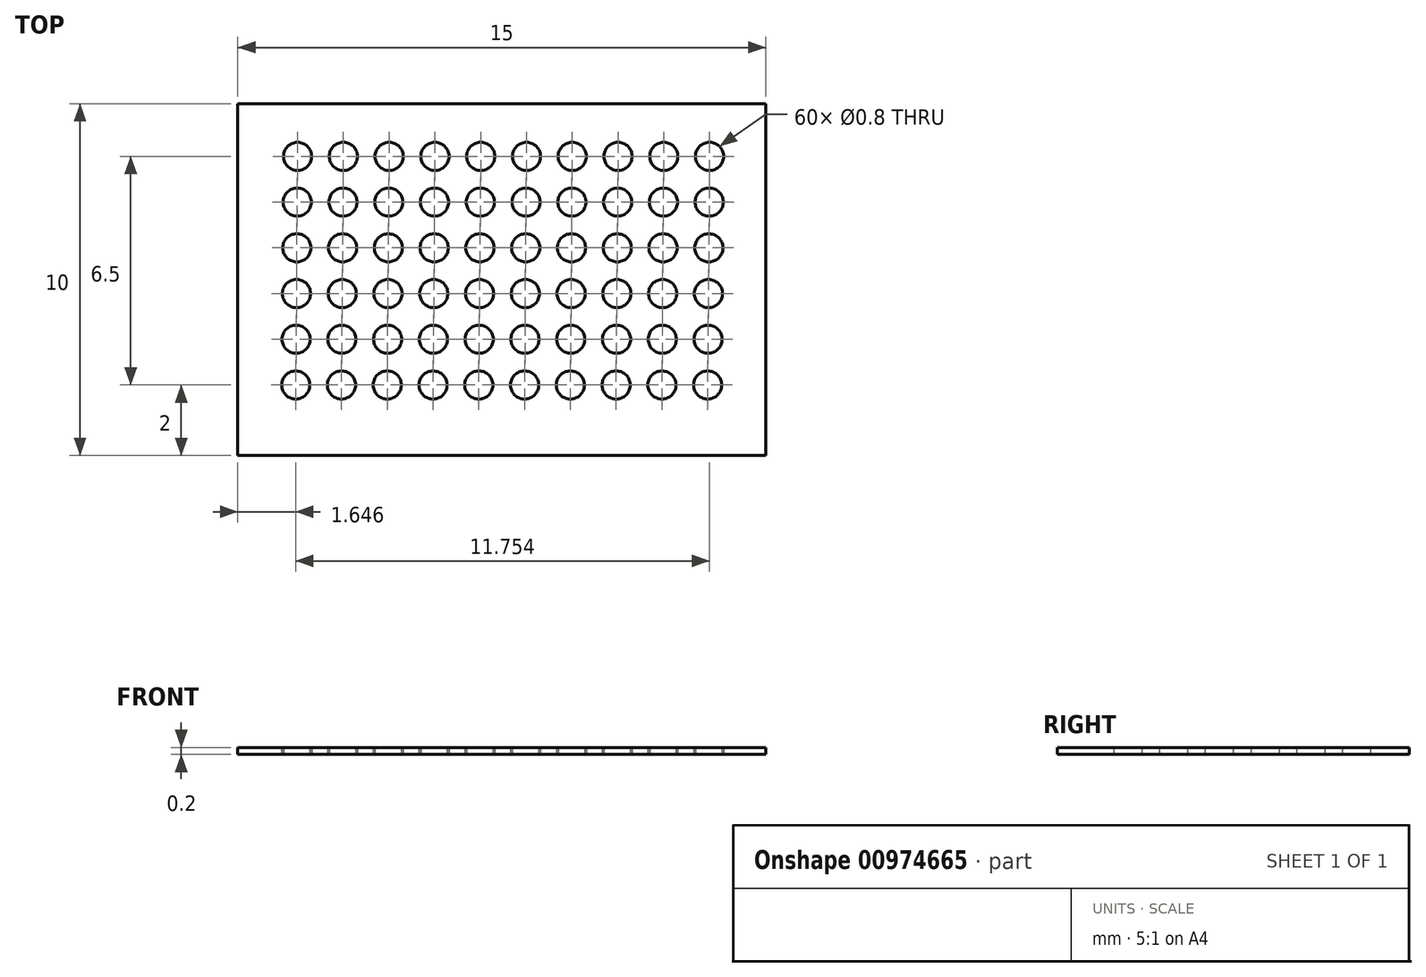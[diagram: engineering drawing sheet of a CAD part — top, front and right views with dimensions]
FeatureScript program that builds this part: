
annotation { "Feature Type Name" : "Feature", "Feature Type Description" : "" }
export const myFeature = defineFeature(function(context is Context, id is Id, definition is map)
    precondition{}
    {
        {
            var Q0;
            Q0=qCreatedBy(makeId("Top.planeOp"),FACE);
            var sketch = newSketch(context, id + "F0", { "sketchPlane" : qUnion([Q0])});
            skLineSegment(sketch, "E0.bottom", {"start": v(0, 0) * mm, "end": v(15, 0) * mm});
            skLineSegment(sketch, "E0.top", {"start": v(0, -10) * mm, "end": v(15, -10) * mm});
            skLineSegment(sketch, "E0.left", {"start": v(0, 0) * mm, "end": v(0, -10) * mm});
            skLineSegment(sketch, "E0.right", {"start": v(15, 0) * mm, "end": v(15, -10) * mm});
            skEllipse(sketch, "E1", {"center": v(1.7, -1.5) * mm, "majorRadius": 0.4 * mm, "minorRadius": 0.4 * mm, "majorAxis": v(0.93, 0.38)});
            skLineSegment(sketch, "E2.direction1", {"start": v(1.7, -1.5) * mm, "end": v(3, -1.5) * mm, "construction": true});
            skLineSegment(sketch, "E3.direction1", {"start": v(1.2, -1.1) * mm, "end": v(1.2, -2) * mm, "construction": true});
            skEllipse(sketch, "E4.0.1.0", {"center": v(3, -1.5) * mm, "majorRadius": 0.4 * mm, "minorRadius": 0.4 * mm, "majorAxis": v(0.93, 0.38)});
            skEllipse(sketch, "E4.0.2.0", {"center": v(4.3, -1.5) * mm, "majorRadius": 0.4 * mm, "minorRadius": 0.4 * mm, "majorAxis": v(0.93, 0.38)});
            skEllipse(sketch, "E4.0.3.0", {"center": v(5.6, -1.5) * mm, "majorRadius": 0.4 * mm, "minorRadius": 0.4 * mm, "majorAxis": v(0.93, 0.38)});
            skEllipse(sketch, "E4.0.4.0", {"center": v(6.9, -1.5) * mm, "majorRadius": 0.4 * mm, "minorRadius": 0.4 * mm, "majorAxis": v(0.93, 0.38)});
            skEllipse(sketch, "E4.0.5.0", {"center": v(8.2, -1.5) * mm, "majorRadius": 0.4 * mm, "minorRadius": 0.4 * mm, "majorAxis": v(0.93, 0.38)});
            skEllipse(sketch, "E4.0.6.0", {"center": v(9.5, -1.5) * mm, "majorRadius": 0.4 * mm, "minorRadius": 0.4 * mm, "majorAxis": v(0.93, 0.38)});
            skEllipse(sketch, "E4.0.7.0", {"center": v(10.8, -1.5) * mm, "majorRadius": 0.4 * mm, "minorRadius": 0.4 * mm, "majorAxis": v(0.93, 0.38)});
            skEllipse(sketch, "E4.0.8.0", {"center": v(12.1, -1.5) * mm, "majorRadius": 0.4 * mm, "minorRadius": 0.4 * mm, "majorAxis": v(0.93, 0.38)});
            skEllipse(sketch, "E4.0.9.0", {"center": v(13.4, -1.5) * mm, "majorRadius": 0.4 * mm, "minorRadius": 0.4 * mm, "majorAxis": v(0.93, 0.38)});
            skEllipse(sketch, "E5.1.0.0", {"center": v(2.99, -2.8) * mm, "majorRadius": 0.4 * mm, "minorRadius": 0.4 * mm, "majorAxis": v(0.93, 0.38)});
            skEllipse(sketch, "E5.1.0.1", {"center": v(1.69, -2.8) * mm, "majorRadius": 0.4 * mm, "minorRadius": 0.4 * mm, "majorAxis": v(0.93, 0.38)});
            skEllipse(sketch, "E5.1.0.2", {"center": v(6.89, -2.8) * mm, "majorRadius": 0.4 * mm, "minorRadius": 0.4 * mm, "majorAxis": v(0.93, 0.38)});
            skLineSegment(sketch, "E5.1.0.3", {"start": v(1.69, -2.8) * mm, "end": v(2.99, -2.8) * mm, "construction": true});
            skEllipse(sketch, "E5.1.0.4", {"center": v(4.29, -2.8) * mm, "majorRadius": 0.4 * mm, "minorRadius": 0.4 * mm, "majorAxis": v(0.93, 0.38)});
            skEllipse(sketch, "E5.1.0.5", {"center": v(9.49, -2.8) * mm, "majorRadius": 0.4 * mm, "minorRadius": 0.4 * mm, "majorAxis": v(0.93, 0.38)});
            skEllipse(sketch, "E5.1.0.6", {"center": v(10.79, -2.8) * mm, "majorRadius": 0.4 * mm, "minorRadius": 0.4 * mm, "majorAxis": v(0.93, 0.38)});
            skEllipse(sketch, "E5.1.0.7", {"center": v(8.19, -2.8) * mm, "majorRadius": 0.4 * mm, "minorRadius": 0.4 * mm, "majorAxis": v(0.93, 0.38)});
            skEllipse(sketch, "E5.1.0.9", {"center": v(5.59, -2.8) * mm, "majorRadius": 0.4 * mm, "minorRadius": 0.4 * mm, "majorAxis": v(0.93, 0.38)});
            skEllipse(sketch, "E5.1.0.10", {"center": v(13.39, -2.8) * mm, "majorRadius": 0.4 * mm, "minorRadius": 0.4 * mm, "majorAxis": v(0.93, 0.38)});
            skEllipse(sketch, "E5.1.0.11", {"center": v(12.09, -2.8) * mm, "majorRadius": 0.4 * mm, "minorRadius": 0.4 * mm, "majorAxis": v(0.93, 0.38)});
            skLineSegment(sketch, "E5.1.0.12", {"start": v(1.2, -2.4) * mm, "end": v(1.2, -3.3) * mm, "construction": true});
            skEllipse(sketch, "E5.2.0.0", {"center": v(2.98, -4.1) * mm, "majorRadius": 0.4 * mm, "minorRadius": 0.4 * mm, "majorAxis": v(0.93, 0.38)});
            skEllipse(sketch, "E5.2.0.1", {"center": v(1.68, -4.1) * mm, "majorRadius": 0.4 * mm, "minorRadius": 0.4 * mm, "majorAxis": v(0.93, 0.38)});
            skEllipse(sketch, "E5.2.0.2", {"center": v(6.88, -4.1) * mm, "majorRadius": 0.4 * mm, "minorRadius": 0.4 * mm, "majorAxis": v(0.93, 0.38)});
            skLineSegment(sketch, "E5.2.0.3", {"start": v(1.68, -4.1) * mm, "end": v(2.98, -4.1) * mm, "construction": true});
            skEllipse(sketch, "E5.2.0.4", {"center": v(4.28, -4.1) * mm, "majorRadius": 0.4 * mm, "minorRadius": 0.4 * mm, "majorAxis": v(0.93, 0.38)});
            skEllipse(sketch, "E5.2.0.5", {"center": v(9.48, -4.1) * mm, "majorRadius": 0.4 * mm, "minorRadius": 0.4 * mm, "majorAxis": v(0.93, 0.38)});
            skEllipse(sketch, "E5.2.0.6", {"center": v(10.78, -4.1) * mm, "majorRadius": 0.4 * mm, "minorRadius": 0.4 * mm, "majorAxis": v(0.93, 0.38)});
            skEllipse(sketch, "E5.2.0.7", {"center": v(8.18, -4.1) * mm, "majorRadius": 0.4 * mm, "minorRadius": 0.4 * mm, "majorAxis": v(0.93, 0.38)});
            skEllipse(sketch, "E5.2.0.9", {"center": v(5.58, -4.1) * mm, "majorRadius": 0.4 * mm, "minorRadius": 0.4 * mm, "majorAxis": v(0.93, 0.38)});
            skEllipse(sketch, "E5.2.0.10", {"center": v(13.38, -4.1) * mm, "majorRadius": 0.4 * mm, "minorRadius": 0.4 * mm, "majorAxis": v(0.93, 0.38)});
            skEllipse(sketch, "E5.2.0.11", {"center": v(12.08, -4.1) * mm, "majorRadius": 0.4 * mm, "minorRadius": 0.4 * mm, "majorAxis": v(0.93, 0.38)});
            skLineSegment(sketch, "E5.2.0.12", {"start": v(1.18, -3.7) * mm, "end": v(1.18, -4.6) * mm, "construction": true});
            skEllipse(sketch, "E5.3.0.0", {"center": v(2.97, -5.4) * mm, "majorRadius": 0.4 * mm, "minorRadius": 0.4 * mm, "majorAxis": v(0.93, 0.38)});
            skEllipse(sketch, "E5.3.0.1", {"center": v(1.67, -5.4) * mm, "majorRadius": 0.4 * mm, "minorRadius": 0.4 * mm, "majorAxis": v(0.93, 0.38)});
            skEllipse(sketch, "E5.3.0.2", {"center": v(6.87, -5.4) * mm, "majorRadius": 0.4 * mm, "minorRadius": 0.4 * mm, "majorAxis": v(0.93, 0.38)});
            skLineSegment(sketch, "E5.3.0.3", {"start": v(1.67, -5.4) * mm, "end": v(2.97, -5.4) * mm, "construction": true});
            skEllipse(sketch, "E5.3.0.4", {"center": v(4.27, -5.4) * mm, "majorRadius": 0.4 * mm, "minorRadius": 0.4 * mm, "majorAxis": v(0.93, 0.38)});
            skEllipse(sketch, "E5.3.0.5", {"center": v(9.47, -5.4) * mm, "majorRadius": 0.4 * mm, "minorRadius": 0.4 * mm, "majorAxis": v(0.93, 0.38)});
            skEllipse(sketch, "E5.3.0.6", {"center": v(10.77, -5.4) * mm, "majorRadius": 0.4 * mm, "minorRadius": 0.4 * mm, "majorAxis": v(0.93, 0.38)});
            skEllipse(sketch, "E5.3.0.7", {"center": v(8.17, -5.4) * mm, "majorRadius": 0.4 * mm, "minorRadius": 0.4 * mm, "majorAxis": v(0.93, 0.38)});
            skEllipse(sketch, "E5.3.0.9", {"center": v(5.57, -5.4) * mm, "majorRadius": 0.4 * mm, "minorRadius": 0.4 * mm, "majorAxis": v(0.93, 0.38)});
            skEllipse(sketch, "E5.3.0.10", {"center": v(13.37, -5.4) * mm, "majorRadius": 0.4 * mm, "minorRadius": 0.4 * mm, "majorAxis": v(0.93, 0.38)});
            skEllipse(sketch, "E5.3.0.11", {"center": v(12.07, -5.4) * mm, "majorRadius": 0.4 * mm, "minorRadius": 0.4 * mm, "majorAxis": v(0.93, 0.38)});
            skLineSegment(sketch, "E5.3.0.12", {"start": v(1.17, -5) * mm, "end": v(1.17, -5.9) * mm, "construction": true});
            skEllipse(sketch, "E5.4.0.0", {"center": v(2.96, -6.7) * mm, "majorRadius": 0.4 * mm, "minorRadius": 0.4 * mm, "majorAxis": v(0.93, 0.38)});
            skEllipse(sketch, "E5.4.0.1", {"center": v(1.66, -6.7) * mm, "majorRadius": 0.4 * mm, "minorRadius": 0.4 * mm, "majorAxis": v(0.93, 0.38)});
            skEllipse(sketch, "E5.4.0.2", {"center": v(6.86, -6.7) * mm, "majorRadius": 0.4 * mm, "minorRadius": 0.4 * mm, "majorAxis": v(0.93, 0.38)});
            skLineSegment(sketch, "E5.4.0.3", {"start": v(1.66, -6.7) * mm, "end": v(2.96, -6.7) * mm, "construction": true});
            skEllipse(sketch, "E5.4.0.4", {"center": v(4.26, -6.7) * mm, "majorRadius": 0.4 * mm, "minorRadius": 0.4 * mm, "majorAxis": v(0.93, 0.38)});
            skEllipse(sketch, "E5.4.0.5", {"center": v(9.46, -6.7) * mm, "majorRadius": 0.4 * mm, "minorRadius": 0.4 * mm, "majorAxis": v(0.93, 0.38)});
            skEllipse(sketch, "E5.4.0.6", {"center": v(10.76, -6.7) * mm, "majorRadius": 0.4 * mm, "minorRadius": 0.4 * mm, "majorAxis": v(0.93, 0.38)});
            skEllipse(sketch, "E5.4.0.7", {"center": v(8.16, -6.7) * mm, "majorRadius": 0.4 * mm, "minorRadius": 0.4 * mm, "majorAxis": v(0.93, 0.38)});
            skEllipse(sketch, "E5.4.0.9", {"center": v(5.56, -6.7) * mm, "majorRadius": 0.4 * mm, "minorRadius": 0.4 * mm, "majorAxis": v(0.93, 0.38)});
            skEllipse(sketch, "E5.4.0.10", {"center": v(13.36, -6.7) * mm, "majorRadius": 0.4 * mm, "minorRadius": 0.4 * mm, "majorAxis": v(0.93, 0.38)});
            skEllipse(sketch, "E5.4.0.11", {"center": v(12.06, -6.7) * mm, "majorRadius": 0.4 * mm, "minorRadius": 0.4 * mm, "majorAxis": v(0.93, 0.38)});
            skLineSegment(sketch, "E5.4.0.12", {"start": v(1.16, -6.3) * mm, "end": v(1.16, -7.2) * mm, "construction": true});
            skEllipse(sketch, "E5.5.0.0", {"center": v(2.95, -8) * mm, "majorRadius": 0.4 * mm, "minorRadius": 0.4 * mm, "majorAxis": v(0.93, 0.38)});
            skEllipse(sketch, "E5.5.0.1", {"center": v(1.65, -8) * mm, "majorRadius": 0.4 * mm, "minorRadius": 0.4 * mm, "majorAxis": v(0.93, 0.38)});
            skEllipse(sketch, "E5.5.0.2", {"center": v(6.85, -8) * mm, "majorRadius": 0.4 * mm, "minorRadius": 0.4 * mm, "majorAxis": v(0.93, 0.38)});
            skLineSegment(sketch, "E5.5.0.3", {"start": v(1.65, -8) * mm, "end": v(2.95, -8) * mm, "construction": true});
            skEllipse(sketch, "E5.5.0.4", {"center": v(4.25, -8) * mm, "majorRadius": 0.4 * mm, "minorRadius": 0.4 * mm, "majorAxis": v(0.93, 0.38)});
            skEllipse(sketch, "E5.5.0.5", {"center": v(9.45, -8) * mm, "majorRadius": 0.4 * mm, "minorRadius": 0.4 * mm, "majorAxis": v(0.93, 0.38)});
            skEllipse(sketch, "E5.5.0.6", {"center": v(10.75, -8) * mm, "majorRadius": 0.4 * mm, "minorRadius": 0.4 * mm, "majorAxis": v(0.93, 0.38)});
            skEllipse(sketch, "E5.5.0.7", {"center": v(8.15, -8) * mm, "majorRadius": 0.4 * mm, "minorRadius": 0.4 * mm, "majorAxis": v(0.93, 0.38)});
            skEllipse(sketch, "E5.5.0.9", {"center": v(5.55, -8) * mm, "majorRadius": 0.4 * mm, "minorRadius": 0.4 * mm, "majorAxis": v(0.93, 0.38)});
            skEllipse(sketch, "E5.5.0.10", {"center": v(13.35, -8) * mm, "majorRadius": 0.4 * mm, "minorRadius": 0.4 * mm, "majorAxis": v(0.93, 0.38)});
            skEllipse(sketch, "E5.5.0.11", {"center": v(12.05, -8) * mm, "majorRadius": 0.4 * mm, "minorRadius": 0.4 * mm, "majorAxis": v(0.93, 0.38)});
            skLineSegment(sketch, "E5.5.0.12", {"start": v(1.15, -7.6) * mm, "end": v(1.15, -8.5) * mm, "construction": true});
            skLineSegment(sketch, "E5.direction1", {"start": v(1.2, -2) * mm, "end": v(1.2, -3.3) * mm, "construction": true});
            skSolve(sketch);
        }
        {
            var Q0;
            Q0=makeQuery(id+"F0.imprint","IMPRINT",FACE,{"disambiguationData":[TD([[makeQuery(id+"F0.imprint","IMPRINT",EDGE,{"derivedFrom":sQuery(id+"F0.wireOp",EDGE,"E0.bottom")}),-1.0]])]});
            extrude(context, id + "F1", {"entities" : qUnion([Q0]), "depth" : 0.2 * mm, "offsetDistance" : 25.4 * mm});
        }
    });
